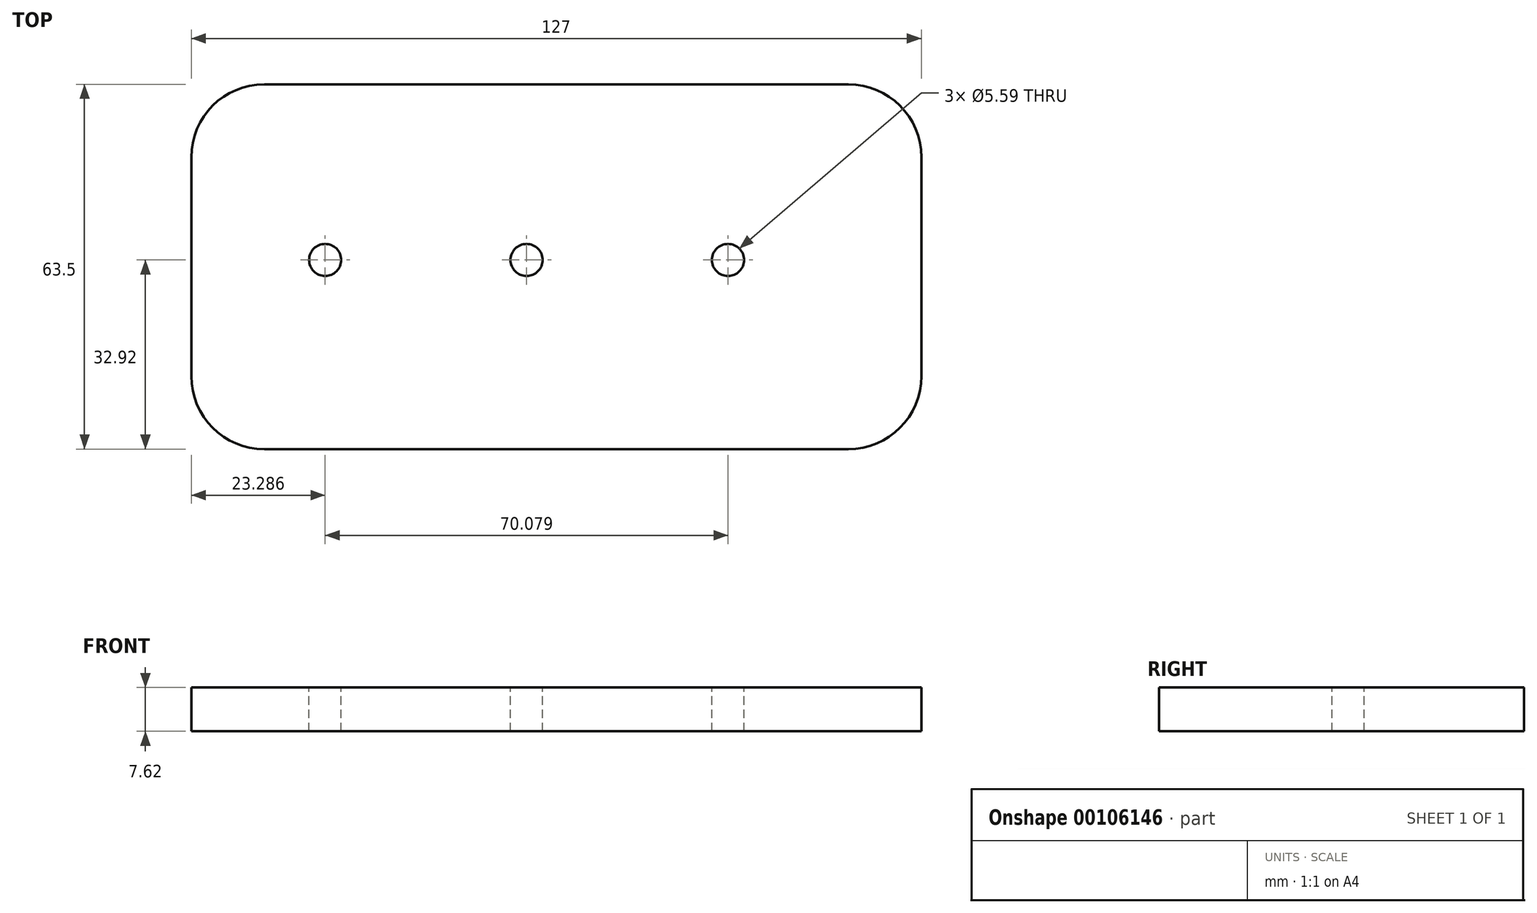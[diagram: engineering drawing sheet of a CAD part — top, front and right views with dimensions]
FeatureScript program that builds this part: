
annotation { "Feature Type Name" : "Feature", "Feature Type Description" : "" }
export const myFeature = defineFeature(function(context is Context, id is Id, definition is map)
    precondition{}
    {
        {
            var Q0;
            Q0=qCreatedBy(makeId("Top.planeOp"),FACE);
            var sketch = newSketch(context, id + "F0", { "sketchPlane" : qUnion([Q0])});
            skLineSegment(sketch, "E0.bottom", {"start": v(-61.2, 30.58) * mm, "end": v(65.8, 30.58) * mm});
            skLineSegment(sketch, "E0.top", {"start": v(-61.2, -32.92) * mm, "end": v(65.8, -32.92) * mm});
            skLineSegment(sketch, "E0.left", {"start": v(-61.2, 30.58) * mm, "end": v(-61.2, -32.92) * mm});
            skLineSegment(sketch, "E0.right", {"start": v(65.8, 30.58) * mm, "end": v(65.8, -32.92) * mm});
            skSolve(sketch);
        }
        {
            var Q0;
            Q0=makeQuery(id+"F0.imprint","IMPRINT",FACE,{"disambiguationData":[TD([[makeQuery(id+"F0.imprint","IMPRINT",EDGE,{"derivedFrom":sQuery(id+"F0.wireOp",EDGE,"E0.bottom")}),-1.0]])]});
            extrude(context, id + "F1", {"entities" : qUnion([Q0]), "depth" : 7.62 * mm});
        }
        {
            var Q0;
            Q0=makeQuery(id+"F1.opExtrude","CAP_FACE",FACE,{"disambiguationData":[OSD([sQuery(id+"F0.wireOp",EDGE,"E0.bottom"),sQuery(id+"F0.wireOp",EDGE,"E0.top"),sQuery(id+"F0.wireOp",EDGE,"E0.left"),sQuery(id+"F0.wireOp",EDGE,"E0.right")])],"isStart":false});
            var sketch = newSketch(context, id + "F2", { "sketchPlane" : qUnion([Q0])});
            skCircle(sketch, "E1", {"center": v(-2.87, 0) * mm, "radius": 2.8 * mm});
            skCircle(sketch, "E2", {"center": v(32.16, 0) * mm, "radius": 2.8 * mm});
            skCircle(sketch, "E3", {"center": v(-37.91, 0) * mm, "radius": 2.8 * mm});
            skSolve(sketch);
        }
        {
            var Q0;
            Q0=makeQuery(id+"F2.imprint","IMPRINT",FACE,{"disambiguationData":[TD([[makeQuery(id+"F2.imprint","IMPRINT",EDGE,{"derivedFrom":sQuery(id+"F2.wireOp",EDGE,"E1")}),1.0]])]});
            var Q1;
            Q1=makeQuery(id+"F2.imprint","IMPRINT",FACE,{"disambiguationData":[TD([[makeQuery(id+"F2.imprint","IMPRINT",EDGE,{"derivedFrom":sQuery(id+"F2.wireOp",EDGE,"E2")}),1.0]])]});
            var Q2;
            Q2=makeQuery(id+"F2.imprint","IMPRINT",FACE,{"disambiguationData":[TD([[makeQuery(id+"F2.imprint","IMPRINT",EDGE,{"derivedFrom":sQuery(id+"F2.wireOp",EDGE,"E3")}),1.0]])]});
            extrude(context, id + "F3", {"entities" : qUnion([Q0, Q1, Q2]), "operationType" : NewBodyOperationType.REMOVE, "oppositeDirection" : true, "depth" : 7.62 * mm});
        }
        {
            var Q0;
            Q0=makeQuery(id+"F1.opExtrude","SWEPT_EDGE",EDGE,{"disambiguationData":[OSD([sQuery(id+"F0.wireOp",EDGE,"E0.top"),sQuery(id+"F0.wireOp",EDGE,"E0.left")])]});
            var Q1;
            Q1=makeQuery(id+"F1.opExtrude","SWEPT_EDGE",EDGE,{"disambiguationData":[OSD([sQuery(id+"F0.wireOp",EDGE,"E0.top"),sQuery(id+"F0.wireOp",EDGE,"E0.right")])]});
            var Q2;
            Q2=makeQuery(id+"F1.opExtrude","SWEPT_EDGE",EDGE,{"disambiguationData":[OSD([sQuery(id+"F0.wireOp",EDGE,"E0.bottom"),sQuery(id+"F0.wireOp",EDGE,"E0.left")])]});
            var Q3;
            Q3=makeQuery(id+"F1.opExtrude","SWEPT_EDGE",EDGE,{"disambiguationData":[OSD([sQuery(id+"F0.wireOp",EDGE,"E0.bottom"),sQuery(id+"F0.wireOp",EDGE,"E0.right")])]});
            fillet(context, id + "F4", {"entities" : qUnion([Q0, Q1, Q2, Q3]), "radius" : 12.7 * mm, "tangentPropagation" : true, "allowEdgeOverflow" : false});
        }
    });
